# Revit family: Faucet-Tub_and_Whirlpool-Delta-Tesla-X552_and_X752
name_source: partatom
category: Plumbing Fixtures
revit_build: Autodesk Revit MEP 2012 (Build: 20110916_2132(x64)
units: mm (PartAtom-declared; Revit-internal decimal feet)

## types (4) — shared parameters
Cold Water Radius = 0.188 "
Cold Water Supply Flow = 0 GPM
Date Modified = January 5, 2015
Depth = 11 "
Equipment Abbreviation = FT
Family Version = 1.0
Hot Water Radius = 0.188 "
Hot Water Supply Flow = 0 GPM
Manufacturer = Delta Faucet Company
Model Disclaimer = Contact Delta Faucet Company for More Information
Pipe Connection Radius = 0.5 "
Product Material = Steel - Delta Faucet Company - Stainless
URL = http://www.deltafaucet.com

## per-type parameters (varying)
| type | Description | Height | Model | zz Integer 1 |
| Roman Tub Widespread 8 - 16 Inch, Three Hole Installation | Tesla Roman Tub/Whirlpool Faucet Trim, 8-16 Inch Widespread 3 Hole Application | 7.5 " | T2752 | 2752 |
| Roman Tub Widespread 8 - 16 Inch, Four Hole Installation | Tesla Roman Tub/Whirlpool Faucet Trim, 8-16 Inch Widespread 4 Hole Application With Hand Shower | 10.125 " | T4752 | 4752 |
| Centerset 4 Inch | Tesla Lavatory Faucet, 4 Inch Centerset 3 Hole Application | 7.5 " | 2252-MPU-DST | 2552 |
| Widespread 4 - 16 Inch | Tesla Lavatory Faucet, 4-16  Inch Widespread 3 Hole Application | 7.5 " | 3552-MPU-DST | 3552 |

## geometry (parser evidence)
native form markers: Sweep x2
no freeform markers — native parametric forms only
